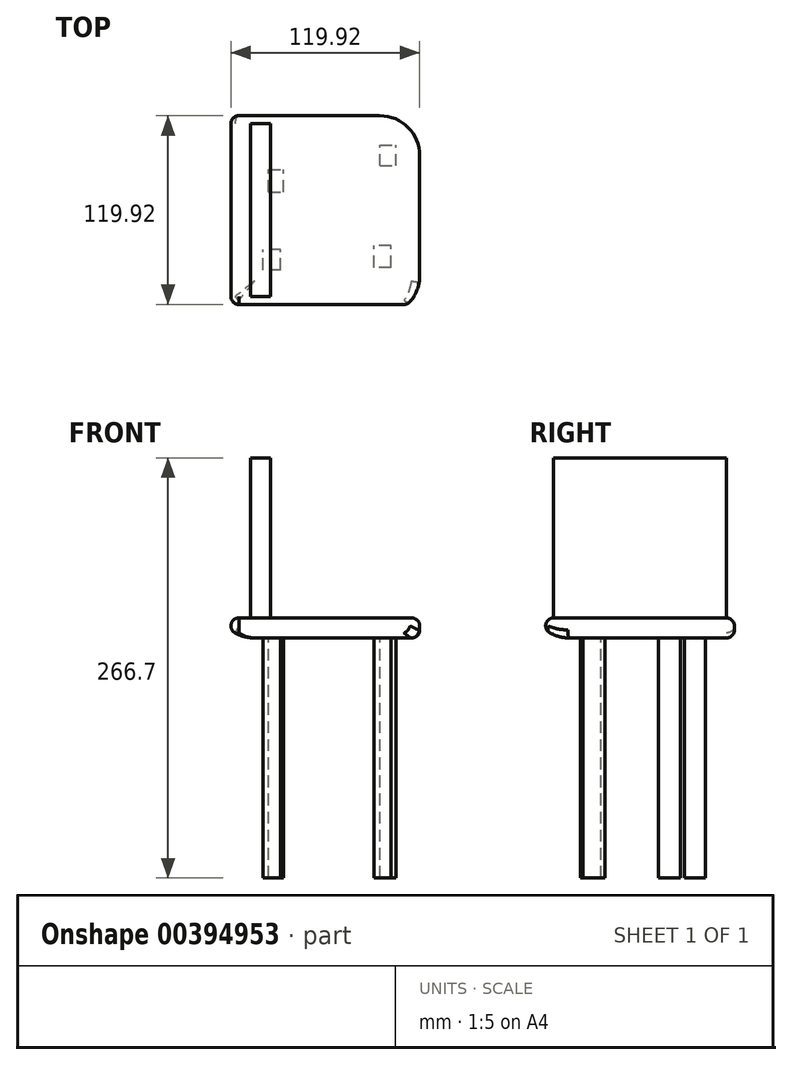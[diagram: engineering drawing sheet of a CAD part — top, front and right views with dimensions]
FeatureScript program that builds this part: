
annotation { "Feature Type Name" : "Feature", "Feature Type Description" : "" }
export const myFeature = defineFeature(function(context is Context, id is Id, definition is map)
    precondition{}
    {
        {
            var Q0;
            Q0=qCreatedBy(makeId("Top.planeOp"),FACE);
            var sketch = newSketch(context, id + "F0", { "sketchPlane" : qUnion([Q0])});
            skLineSegment(sketch, "E0.bottom", {"start": v(0, 0) * mm, "end": v(127, 0) * mm});
            skLineSegment(sketch, "E0.top", {"start": v(0, 127) * mm, "end": v(127, 127) * mm});
            skLineSegment(sketch, "E0.left", {"start": v(0, 0) * mm, "end": v(0, 127) * mm});
            skLineSegment(sketch, "E0.right", {"start": v(127, 0) * mm, "end": v(127, 127) * mm});
            skSolve(sketch);
        }
        {
            var Q0;
            Q0=makeQuery(id+"F0.imprint","IMPRINT",FACE,{"disambiguationData":[TD([[makeQuery(id+"F0.imprint","IMPRINT",EDGE,{"derivedFrom":sQuery(id+"F0.wireOp",EDGE,"E0.bottom")}),1.0]])]});
            extrude(context, id + "F1", {"entities" : qUnion([Q0]), "depth" : 12.7 * mm});
        }
        {
            var Q0;
            Q0=makeQuery(id+"F1.opExtrude","SWEPT_EDGE",EDGE,{"disambiguationData":[OSD([sQuery(id+"F0.wireOp",EDGE,"E0.bottom"),sQuery(id+"F0.wireOp",EDGE,"E0.right")])]});
            var Q1;
            Q1=makeQuery(id+"F1.opExtrude","SWEPT_EDGE",EDGE,{"disambiguationData":[OSD([sQuery(id+"F0.wireOp",EDGE,"E0.top"),sQuery(id+"F0.wireOp",EDGE,"E0.right")])]});
            var Q2;
            Q2=makeQuery(id+"F1.opExtrude","CAP_EDGE",EDGE,{"disambiguationData":[OSD([sQuery(id+"F0.wireOp",EDGE,"E0.left")])],"isStart":true});
            var Q3;
            Q3=makeQuery(id+"F1.opExtrude","CAP_EDGE",EDGE,{"disambiguationData":[OSD([sQuery(id+"F0.wireOp",EDGE,"E0.bottom")])],"isStart":true});
            fillet(context, id + "F2", {"entities" : qUnion([Q0, Q1, Q2, Q3]), "radius" : 25.4 * mm, "tangentPropagation" : true, "allowEdgeOverflow" : false});
        }
        {
            var Q0;
            Q0=makeQuery(id+"F2.opFillet","BLEND_EDGE",EDGE,{"blendedFrom":[makeQuery(id+"F1.opExtrude","CAP_EDGE",EDGE,{"disambiguationData":[OSD([sQuery(id+"F0.wireOp",EDGE,"E0.left")])],"isStart":true}),makeQuery(id+"F1.opExtrude","SWEPT_FACE",FACE,{"disambiguationData":[OSD([sQuery(id+"F0.wireOp",EDGE,"E0.top")])]})],"blendedInto":[makeQuery(id+"F1.opExtrude","SWEPT_FACE",FACE,{"disambiguationData":[OSD([sQuery(id+"F0.wireOp",EDGE,"E0.top")])]})]});
            fillet(context, id + "F3", {"entities" : qUnion([Q0]), "radius" : 5.08 * mm, "tangentPropagation" : true, "allowEdgeOverflow" : false});
        }
        {
            var Q0;
            Q0=makeQuery(id+"F2.opFillet","BLEND_EDGE",EDGE,{"blendedFrom":[makeQuery(id+"F1.opExtrude","CAP_EDGE",EDGE,{"disambiguationData":[OSD([sQuery(id+"F0.wireOp",EDGE,"E0.bottom")])],"isStart":true}),makeQuery(id+"F1.opExtrude","CAP_EDGE",EDGE,{"disambiguationData":[OSD([sQuery(id+"F0.wireOp",EDGE,"E0.left")])],"isStart":true})],"blendedInto":[]});
            var Q1;
            Q1=makeQuery(id+"F1.opExtrude","CAP_FACE",FACE,{"disambiguationData":[OSD([sQuery(id+"F0.wireOp",EDGE,"E0.bottom"),sQuery(id+"F0.wireOp",EDGE,"E0.top"),sQuery(id+"F0.wireOp",EDGE,"E0.left"),sQuery(id+"F0.wireOp",EDGE,"E0.right")])],"isStart":false});
            fillet(context, id + "F4", {"entities" : qUnion([Q0, Q1]), "radius" : 5.08 * mm, "tangentPropagation" : true, "allowEdgeOverflow" : false});
        }
        {
            var Q0;
            Q0=makeQuery(id+"F1.opExtrude","CAP_FACE",FACE,{"disambiguationData":[OSD([sQuery(id+"F0.wireOp",EDGE,"E0.bottom"),sQuery(id+"F0.wireOp",EDGE,"E0.top"),sQuery(id+"F0.wireOp",EDGE,"E0.left"),sQuery(id+"F0.wireOp",EDGE,"E0.right")])],"isStart":true});
            var sketch = newSketch(context, id + "F5", { "sketchPlane" : qUnion([Q0])});
            skLineSegment(sketch, "E1.bottom", {"start": v(101.9, -95.14) * mm, "end": v(111.93, -95.14) * mm});
            skLineSegment(sketch, "E1.top", {"start": v(101.9, -108.44) * mm, "end": v(111.93, -108.44) * mm});
            skLineSegment(sketch, "E1.left", {"start": v(101.9, -95.14) * mm, "end": v(101.9, -108.44) * mm});
            skLineSegment(sketch, "E1.right", {"start": v(111.93, -95.14) * mm, "end": v(111.93, -108.44) * mm});
            skSolve(sketch);
        }
        {
            var Q0;
            Q0=makeQuery(id+"F5.imprint","IMPRINT",FACE,{"disambiguationData":[TD([[makeQuery(id+"F5.imprint","IMPRINT",EDGE,{"derivedFrom":sQuery(id+"F5.wireOp",EDGE,"E1.bottom")}),-1.0]])]});
            extrude(context, id + "F6", {"entities" : qUnion([Q0]), "operationType" : NewBodyOperationType.ADD, "depth" : 152.4 * mm});
        }
        {
            var Q0;
            Q0=makeQuery(id+"F1.opExtrude","CAP_FACE",FACE,{"disambiguationData":[OSD([sQuery(id+"F0.wireOp",EDGE,"E0.bottom"),sQuery(id+"F0.wireOp",EDGE,"E0.top"),sQuery(id+"F0.wireOp",EDGE,"E0.left"),sQuery(id+"F0.wireOp",EDGE,"E0.right")])],"isStart":true});
            var sketch = newSketch(context, id + "F7", { "sketchPlane" : qUnion([Q0])});
            skLineSegment(sketch, "E2.bottom", {"start": v(31, -78.6) * mm, "end": v(40.54, -78.6) * mm});
            skLineSegment(sketch, "E2.top", {"start": v(31, -92.67) * mm, "end": v(40.54, -92.67) * mm});
            skLineSegment(sketch, "E2.left", {"start": v(31, -78.6) * mm, "end": v(31, -92.67) * mm});
            skLineSegment(sketch, "E2.right", {"start": v(40.54, -78.6) * mm, "end": v(40.54, -92.67) * mm});
            skSolve(sketch);
        }
        {
            var Q0;
            Q0=makeQuery(id+"F7.imprint","IMPRINT",FACE,{"disambiguationData":[TD([[makeQuery(id+"F7.imprint","IMPRINT",EDGE,{"derivedFrom":sQuery(id+"F7.wireOp",EDGE,"E2.bottom")}),-1.0]])]});
            extrude(context, id + "F8", {"entities" : qUnion([Q0]), "operationType" : NewBodyOperationType.ADD, "depth" : 152.4 * mm});
        }
        {
            var Q0;
            Q0=makeQuery(id+"F1.opExtrude","CAP_FACE",FACE,{"disambiguationData":[OSD([sQuery(id+"F0.wireOp",EDGE,"E0.bottom"),sQuery(id+"F0.wireOp",EDGE,"E0.top"),sQuery(id+"F0.wireOp",EDGE,"E0.left"),sQuery(id+"F0.wireOp",EDGE,"E0.right")])],"isStart":true});
            var sketch = newSketch(context, id + "F9", { "sketchPlane" : qUnion([Q0])});
            skLineSegment(sketch, "E3.bottom", {"start": v(38.62, -29.02) * mm, "end": v(27.52, -29.02) * mm});
            skLineSegment(sketch, "E3.top", {"start": v(38.62, -42.1) * mm, "end": v(27.52, -42.1) * mm});
            skLineSegment(sketch, "E3.left", {"start": v(38.62, -29.02) * mm, "end": v(38.62, -42.1) * mm});
            skLineSegment(sketch, "E3.right", {"start": v(27.52, -29.02) * mm, "end": v(27.52, -42.1) * mm});
            skSolve(sketch);
        }
        {
            var Q0;
            Q0=makeQuery(id+"F9.imprint","IMPRINT",FACE,{"disambiguationData":[TD([[makeQuery(id+"F9.imprint","IMPRINT",EDGE,{"derivedFrom":sQuery(id+"F9.wireOp",EDGE,"E3.bottom")}),1.0]])]});
            extrude(context, id + "F10", {"entities" : qUnion([Q0]), "operationType" : NewBodyOperationType.ADD, "depth" : 152.4 * mm});
        }
        {
            var Q0;
            Q0=makeQuery(id+"F1.opExtrude","CAP_FACE",FACE,{"disambiguationData":[OSD([sQuery(id+"F0.wireOp",EDGE,"E0.bottom"),sQuery(id+"F0.wireOp",EDGE,"E0.top"),sQuery(id+"F0.wireOp",EDGE,"E0.left"),sQuery(id+"F0.wireOp",EDGE,"E0.right")])],"isStart":true});
            var sketch = newSketch(context, id + "F11", { "sketchPlane" : qUnion([Q0])});
            skLineSegment(sketch, "E4.bottom", {"start": v(108.78, -30.64) * mm, "end": v(97.8, -30.64) * mm});
            skLineSegment(sketch, "E4.top", {"start": v(108.78, -44.6) * mm, "end": v(97.8, -44.6) * mm});
            skLineSegment(sketch, "E4.left", {"start": v(108.78, -30.64) * mm, "end": v(108.78, -44.6) * mm});
            skLineSegment(sketch, "E4.right", {"start": v(97.8, -30.64) * mm, "end": v(97.8, -44.6) * mm});
            skSolve(sketch);
        }
        {
            var Q0;
            Q0=makeQuery(id+"F11.imprint","IMPRINT",FACE,{"disambiguationData":[TD([[makeQuery(id+"F11.imprint","IMPRINT",EDGE,{"derivedFrom":sQuery(id+"F11.wireOp",EDGE,"E4.bottom")}),1.0]])]});
            extrude(context, id + "F12", {"entities" : qUnion([Q0]), "operationType" : NewBodyOperationType.ADD, "depth" : 152.4 * mm});
        }
        {
            var Q0;
            Q0=makeQuery(id+"F1.opExtrude","CAP_FACE",FACE,{"disambiguationData":[OSD([sQuery(id+"F0.wireOp",EDGE,"E0.bottom"),sQuery(id+"F0.wireOp",EDGE,"E0.top"),sQuery(id+"F0.wireOp",EDGE,"E0.left"),sQuery(id+"F0.wireOp",EDGE,"E0.right")])],"isStart":false});
            var sketch = newSketch(context, id + "F13", { "sketchPlane" : qUnion([Q0])});
            skLineSegment(sketch, "E5.bottom", {"start": v(12.16, 12.16) * mm, "end": v(19.5, 12.16) * mm});
            skLineSegment(sketch, "E5.top", {"start": v(12.16, 121.92) * mm, "end": v(19.5, 121.92) * mm});
            skLineSegment(sketch, "E5.left", {"start": v(12.16, 12.16) * mm, "end": v(12.16, 121.92) * mm});
            skLineSegment(sketch, "E5.right", {"start": v(19.5, 12.16) * mm, "end": v(19.5, 121.92) * mm});
            skSolve(sketch);
        }
        {
            var Q0;
            Q0=sQuery(id+"F13.wireOp",EDGE,"E5.right");
            extrude(context, id + "F14", {"bodyType" : ToolBodyType.SURFACE, "surfaceEntities" : qUnion([Q0]), "depth" : 101.6 * mm});
        }
        {
            var Q0;
            Q0=makeQuery(id+"F14.opExtrude","SWEPT_FACE",FACE,{"disambiguationData":[OSD([sQuery(id+"F13.wireOp",EDGE,"E5.right")])]});
            var sketch = newSketch(context, id + "F15", { "sketchPlane" : qUnion([Q0])});
            skLineSegment(sketch, "E6.bottom", {"start": v(12.16, 114.3) * mm, "end": v(121.92, 114.3) * mm});
            skLineSegment(sketch, "E6.top", {"start": v(12.16, 12.7) * mm, "end": v(121.92, 12.7) * mm});
            skLineSegment(sketch, "E6.left", {"start": v(12.16, 114.3) * mm, "end": v(12.16, 12.7) * mm});
            skLineSegment(sketch, "E6.right", {"start": v(121.92, 114.3) * mm, "end": v(121.92, 12.7) * mm});
            skSolve(sketch);
        }
        {
            var Q0;
            Q0=makeQuery(id+"F15.imprint","IMPRINT",FACE,{"disambiguationData":[TD([[makeQuery(id+"F15.imprint","IMPRINT",EDGE,{"derivedFrom":sQuery(id+"F15.wireOp",EDGE,"E6.bottom")}),-1.0]])]});
            extrude(context, id + "F16", {"entities" : qUnion([Q0]), "operationType" : NewBodyOperationType.ADD, "depth" : 12.7 * mm});
        }
    });
